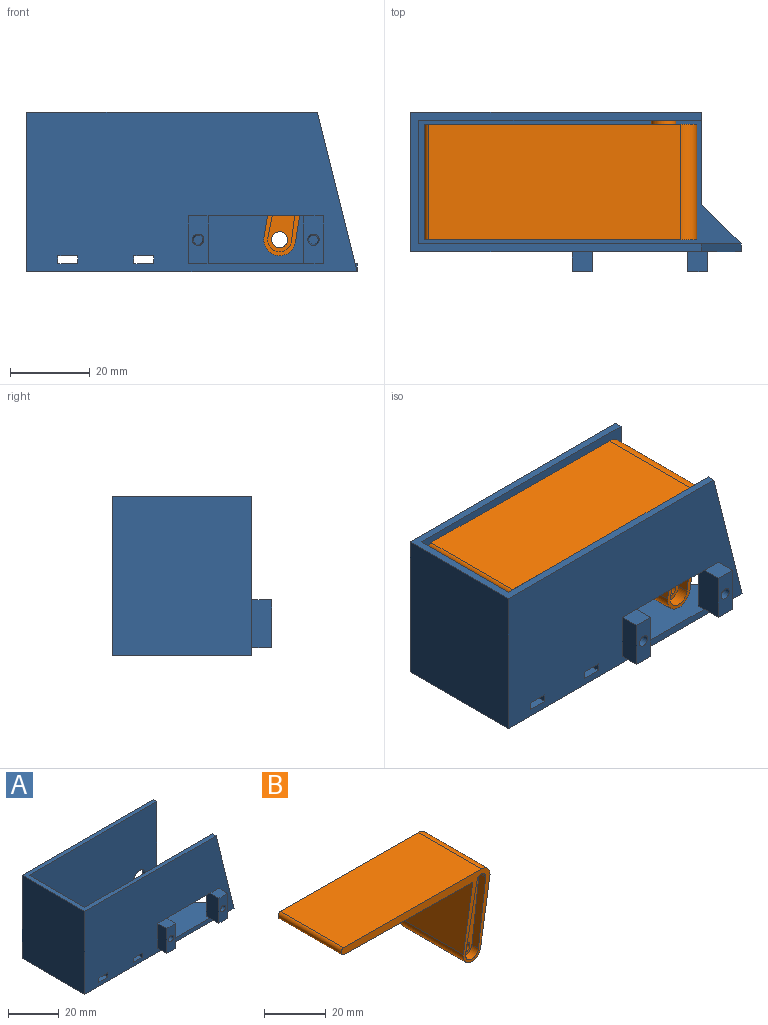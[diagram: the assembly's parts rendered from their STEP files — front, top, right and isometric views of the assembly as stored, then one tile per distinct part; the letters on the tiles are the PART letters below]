
ASSEMBLY  parts=2 mates=1
PART A: 41 faces, bbox 83x40x40 mm
  f0: plane 83x40mm, normal (0,-1,0), area 2692mm2, adj f6,f7,f8,f9,f10,f14,f15,f16
  f1: plane 80.5x38mm, normal (0,1,0), area 2570.5mm2, adj f5,f7,f9,f10,f13,f19,f27,f35
  f2: plane 71x38mm, normal (0,-1,0), area 2639.5mm2, adj f4,f5,f7,f9,f28,f29,f30,f31
  f3: plane 73x40mm, normal (0,1,0), area 2861.5mm2, adj f4,f6,f7,f8,f9,f28,f29,f30
  f4: plane 40x23mm, normal (1,0,0), area 122mm2, adj f2,f3,f7,f8,f9,f11
  f5: plane 38x31mm, normal (1,0,0), area 1178mm2, adj f1,f2,f7,f9
  f6: plane 40x35mm, normal (-1,0,0), area 1400mm2, adj f0,f3,f7,f8
  f7: plane 73x35mm, normal (0,0,1), area 354mm2, adj f0,f1,f2,f3,f4,f5,f6,f10
  f8: plane 83x35mm, normal (0,0,-1), area 2625mm2, adj f0,f3,f4,f6,f10,f11
  f9: plane 81x35mm, normal (0,0,1), area 2339mm2, adj f0,f1,f2,f3,f4,f5,f11,f12
  f10: plane 40x10mm, normal (0.97,0,0.24), area 82.5mm2, adj f0,f1,f7,f8,f12
  f11: plane 10x10mm, normal (0.71,0.71,0), area 28.3mm2, adj f4,f8,f9,f12
  f12: plane 2x0.5mm, normal (0,-1,0), area 0.5mm2, adj f9,f10,f11
  f13: plane 12x7mm, normal (-1,0,0), area 84mm2, adj f1,f9,f14,f16,f17,f27
  f14: plane 5x5mm, normal (0,0,-1), area 25mm2, adj f0,f13,f15,f17
  f15: plane 12x5mm, normal (1,0,0), area 60mm2, adj f0,f14,f16,f17
  f16: plane 5x5mm, normal (0,0,1), area 25mm2, adj f0,f13,f15,f17
  f17: plane 12x5mm, normal (0,-1,0), area 53.5mm2, adj f13,f14,f15,f16,f25
  f18: plane 5x5mm, normal (0,0,-1), area 25mm2, adj f0,f19,f21,f22
  f19: plane 12x7mm, normal (1,0,0), area 84mm2, adj f1,f9,f18,f20,f22,f27
  f20: plane 5x5mm, normal (0,0,1), area 25mm2, adj f0,f19,f21,f22
  f21: plane 12x5mm, normal (-1,0,0), area 60mm2, adj f0,f18,f20,f22
  f22: plane 12x5mm, normal (0,-1,0), area 53.5mm2, adj f18,f19,f20,f21,f23
  f23: cone r=1mm half-angle=5deg, axis (0,-1,0), area 24.7mm2, adj f22,f24
  f24: plane 2.35x2.35mm, normal (0,-1,0), area 4.3mm2, adj f23
  f25: cone r=1mm half-angle=5deg, axis (0,-1,0), area 24.7mm2, adj f17,f26
  f26: plane 2.35x2.35mm, normal (0,-1,0), area 4.3mm2, adj f25
  f27: plane 24x2mm, normal (0,0,-1), area 48mm2, adj f0,f1,f13,f19
  f28: cylinder r=3.5mm len=7mm, axis (0,-1,0), area 44mm2, adj f2,f3
  f29: plane 5x2mm, normal (0,0,-1), area 10mm2, adj f2,f3,f30,f31
  f30: plane 2x2mm, normal (-1,0,0), area 4mm2, adj f2,f3,f9,f29
  f31: plane 2x2mm, normal (1,0,0), area 4mm2, adj f2,f3,f9,f29
  f32: plane 5x2mm, normal (0,0,-1), area 10mm2, adj f2,f3,f33,f34
  f33: plane 2x2mm, normal (-1,0,0), area 4mm2, adj f2,f3,f9,f32
  f34: plane 2x2mm, normal (1,0,0), area 4mm2, adj f2,f3,f9,f32
  f35: plane 2x2mm, normal (1,0,0), area 4mm2, adj f0,f1,f9,f37
  f36: plane 2x2mm, normal (-1,0,0), area 4mm2, adj f0,f1,f9,f37
  f37: plane 5x2mm, normal (0,0,-1), area 10mm2, adj f0,f1,f35,f36
  f38: plane 2x2mm, normal (1,0,0), area 4mm2, adj f0,f1,f9,f40
  f39: plane 2x2mm, normal (-1,0,0), area 4mm2, adj f0,f1,f9,f40
  f40: plane 5x2mm, normal (0,0,-1), area 10mm2, adj f0,f1,f38,f39
PART B: 17 faces, bbox 68.4x32x35 mm
  f0: cylinder r=2mm len=29mm, axis (0,-1,0), area 364.4mm2, adj f14,f16
  f1: plane 29x26.66mm, normal (0.99,0,-0.16), area 783mm2, adj f2,f7,f8,f9
  f2: cylinder r=4mm len=29mm, axis (0,-1,0), area 200.1mm2, adj f1,f3,f8,f9
  f3: plane 63.43x29mm, normal (0.01,0,1), area 1839.6mm2, adj f2,f4,f8,f9
  f4: cylinder r=1.5mm len=29mm, axis (0,-1,0), area 121.5mm2, adj f3,f5,f8,f9
  f5: plane 58.99x29mm, normal (-0.01,0,-1), area 1710.8mm2, adj f4,f6,f8,f9
  f6: plane 29x26.66mm, normal (-0.99,0,0.16), area 783mm2, adj f5,f7,f8,f9
  f7: cylinder r=4mm len=29mm, axis (0,-1,0), area 364.4mm2, adj f1,f6,f8,f9
  f8: plane 68.42x35.01mm, normal (0,1,0), area 428.6mm2, adj f1,f2,f3,f4,f5,f6,f7,f15
  f9: plane 68.42x35.01mm, normal (0,-1,0), area 303.3mm2, adj f1,f2,f3,f4,f5,f6,f7,f10
  f10: cylinder r=2mm len=3.96mm, axis (0,-1,0), area 18.4mm2, adj f9,f11,f13,f14
  f11: plane 26.46x5.27mm, normal (0.98,0,-0.2), area 80.9mm2, adj f9,f10,f12,f14
  f12: cylinder r=3mm len=5.98mm, axis (0,-1,0), area 28.9mm2, adj f9,f11,f13,f14
  f13: plane 26.78x3.3mm, normal (-0.99,0,0.12), area 80.9mm2, adj f9,f10,f12,f14
  f14: plane 31.66x9.29mm, normal (0,-1,0), area 142.9mm2, adj f0,f10,f11,f12,f13
  f15: cylinder r=3.1mm len=6.2mm, axis (0,-1,0), area 58.4mm2, adj f8,f16
  f16: plane 6.2x6.2mm, normal (0,1,0), area 17.6mm2, adj f0,f15
PLACE A t=(-6.81,5.79,-0.03)mm fixed
PLACE B rot(axis=(0,1,0),0.1deg) t=(-6.82,5.79,-0.01)mm
MATE revolute A.f28 <-> B.f0  axis (0,1,0) through (19.22,23.29,7.97)mm
